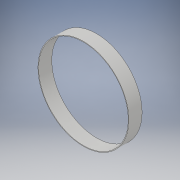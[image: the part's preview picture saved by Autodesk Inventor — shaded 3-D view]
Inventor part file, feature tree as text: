
AUTODESK INVENTOR PART (.ipt)
format: ipt  version: 2019 (Build 230136000, 136)  size: 104,960 bytes
history: native  units: mm
features: extrude x2, sketch x2
ambient origin geometry x8: Origin, YZ Plane, XZ Plane, XY Plane, X Axis, Y Axis, Z Axis, Center Point
bodies: Solid1 (feature_tree)
feature tree (4):
  extrude  "Extrusion1"  Depth=9.45mm TaperAngle=0.0deg
  extrude  "Extrusion2"  Depth=9.45mm TaperAngle=0.0deg
  sketch  "Sketch1"  dims[d0=65.38mm d1=9.45mm d2=0.0mm]
  sketch  "Sketch2"  dims[d3=64.4mm d4=9.45mm d5=0.0mm]
